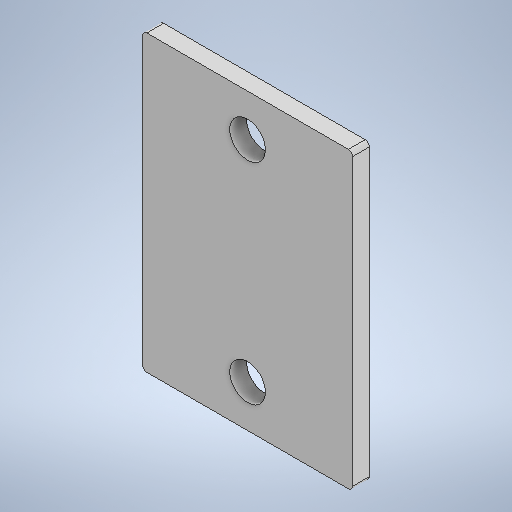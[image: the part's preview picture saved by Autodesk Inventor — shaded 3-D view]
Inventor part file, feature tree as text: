
AUTODESK INVENTOR PART (.ipt)
format: ipt  version: 2025 (Build 290162010, 162A)  size: 243,712 bytes
history: native  units: mm
features: sketch x2, sheet_metal_op x1, hole x1, fillet x1, other x1
ambient origin geometry x8: Origin, YZ Plane, XZ Plane, XY Plane, X Axis, Y Axis, Z Axis, Center Point
bodies: Solid1 (feature_tree)
feature tree (6):
  sheet_metal_op  "Face1"
  hole  "Hole1"  [1 undecoded]
  fillet  "Fillet1"  Radius=8.0mm
  sketch  "Sketch1"  dims[d0=100.0mm d1=140.0mm d2=8.0mm]
  other  "Plate1"
  sketch  "Sketch2"  dims[d3=17.0mm d4=6.0mm d5=4.0mm d6=2.0mm d7=90.0deg d8=8.0mm d9=20.594885mm d16=2.0mm d17=100.0mm]
note: 1 required parameter value undecoded (feature->parameter linkage not recoverable at this tier; creation-order binding heuristic only, values carry confidence <= 0.55)
